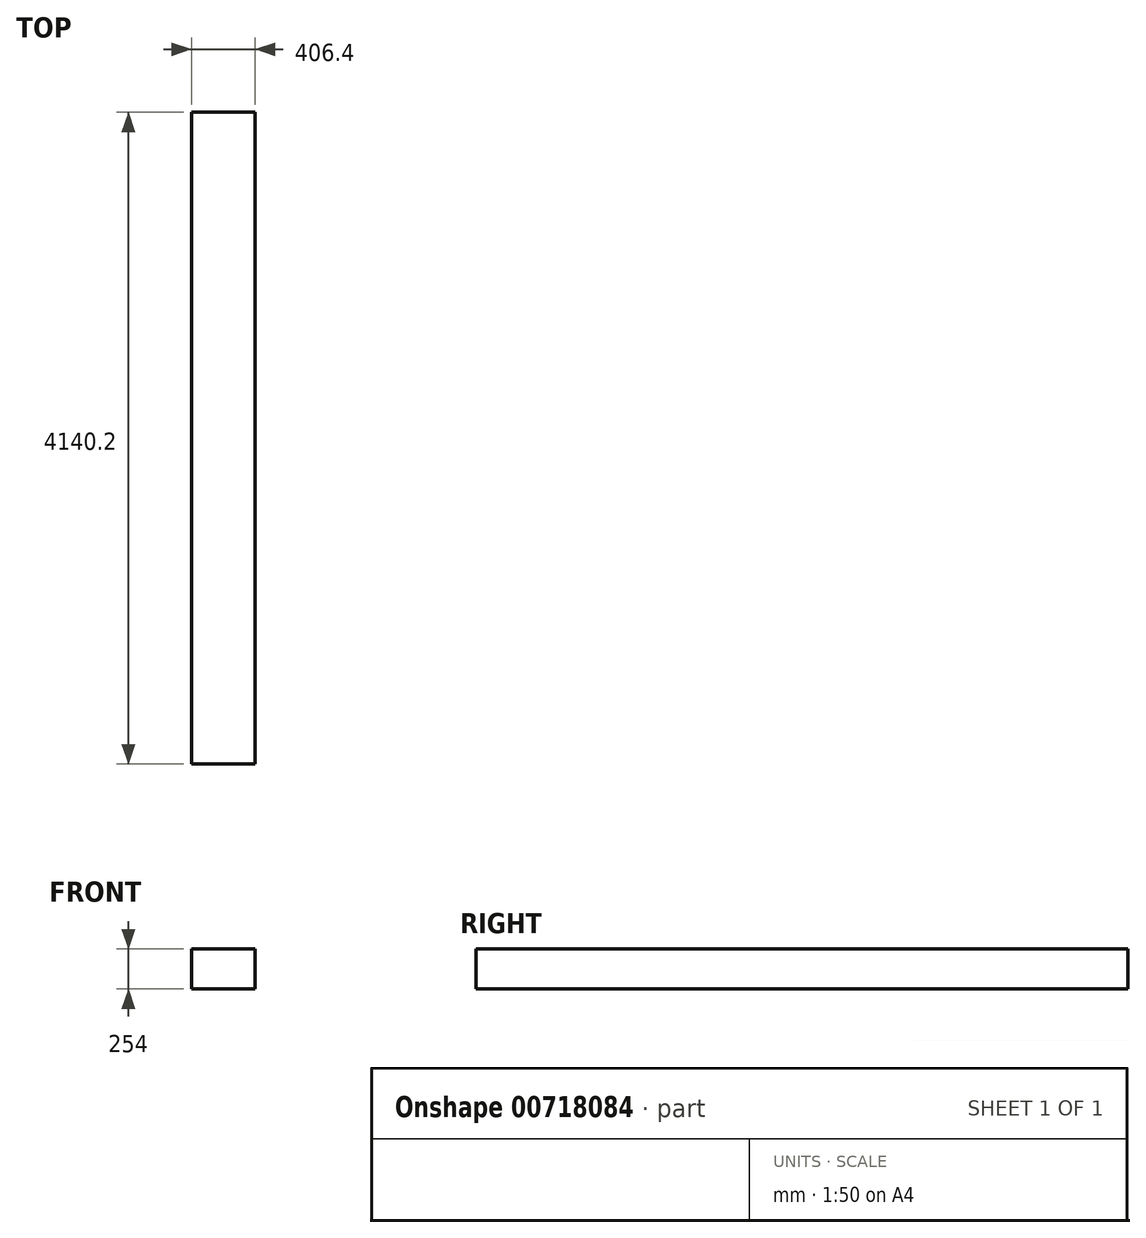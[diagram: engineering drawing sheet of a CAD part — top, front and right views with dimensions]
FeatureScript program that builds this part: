
annotation { "Feature Type Name" : "Feature", "Feature Type Description" : "" }
export const myFeature = defineFeature(function(context is Context, id is Id, definition is map)
    precondition{}
    {
        {
            var Q0;
            Q0=qCreatedBy(makeId("Front.planeOp"),FACE);
            var sketch = newSketch(context, id + "F0", { "sketchPlane" : qUnion([Q0])});
            skLineSegment(sketch, "E0.bottom", {"start": v(203.2, -127) * mm, "end": v(-203.2, -127) * mm});
            skLineSegment(sketch, "E0.top", {"start": v(203.2, 127) * mm, "end": v(-203.2, 127) * mm});
            skLineSegment(sketch, "E0.left", {"start": v(203.2, -127) * mm, "end": v(203.2, 127) * mm});
            skLineSegment(sketch, "E0.right", {"start": v(-203.2, -127) * mm, "end": v(-203.2, 127) * mm});
            skPoint(sketch, "E0.middle", {"position": v(0, 0) * mm});
            skSolve(sketch);
        }
        {
            var Q0;
            Q0 = qSketchRegion(id + "F0", true);
            extrude(context, id + "F1", {"entities" : qUnion([Q0]), "depth" : 4140.2 * mm, "offsetDistance" : 25.4 * mm});
        }
    });
